# Revit family: 0047687 Lighting Fixture_Sylvania_Sylproof Superia LED_Surface Mounted
name_source: partatom
category: Lighting Fixtures
revit_build: Autodesk Revit 2015 (Build: 20140606_1530(x64)
units: mm (PartAtom-declared; Revit-internal decimal feet)

## types (1)
- SYLPROOF SUPERIA LED 665MM SINGLE NW
    Apparent Load = 12 VA
    Assembly Code = D5020200
    Body Material = Polycarbonate_Body_Sylvania_Brite White
    Bracket-Diffuser Material = <By Category>
    Bracket-Mounting Material = <By Category>
    CRI ( Ra ) = 85
    Catalog Number = 0047687 SYLPROOF SUPERIA LED 665MM SINGLE NW

LED
    Color Filter = 16777215
    Default Elevation = 0 mm  [stored 0 ft]
    Description = Weatherproof LED luminaire achieving up to 6,880lm (86lm/W); Linear prisms designed to optimise light output and to reduce glare;Extra long life with 50,000 hours; LED technology provides energy efficient solution and reduced maintenance costs.
    Diffuser Brackets Length = 505 mm  [stored 1.65682 ft]
    Diffuser Material = Polycarbonate_Diffuser_Sylvania_Clear
    Dimming Lamp Color Temperature Shift = <None>
    Emit Shape Visible in Rendering = No
    Emit from Rectangle Length = 645 mm  [stored 2.11614 ft]
    Emit from Rectangle Width = 66 mm
    Height = 98 mm  [stored 0.321522 ft]
    Housing ( Degree ) = 850 C
    IP rating = 65
    LOR Light Output Ratio ( % ) = 100 %
    Lamp = 12W LED
    Lamp - Single = Yes
    Lamp - Twin = No
    Lamp Comments = Integrated LED
    Lamp Material = Acrylic High Luminance Glass_Lamp_Sylvania_White
    Length = 665 mm  [stored 2.18176 ft]
    Length Help = 605 mm  [stored 1.98491 ft]
    Manufacturer = Feilo-Sylvania Group
    Model = SYLPROOF SUPERIA LED 665MM SINGLE NW
    Mounting Brackets Length = 390 mm  [stored 1.27953 ft]
    Mounting Brackets Width = 41 mm  [stored 0.134514 ft]
    Number of Diffuser Brackets = 3
    Photometric Web File = 0047687_SYLPROOFSUPERIALED12W4KNW-163341.ies
    Product Family = Sylproof Susperia LED
    Side Void Width = 45 mm  [stored 0.147638 ft]
    Tilt Angle = -90.00°
    Voltage = 240 V
    Voltage Comments = UNV (Universal Voltage; 220-240 Volt)
    Weight = 1.2 kg
    Width = 94 mm  [stored 0.308399 ft]
    Width Help = 26 mm

note: [stored X ft] marks values corroborated as IEEE doubles in the binary element streams (Revit-internal decimal feet)

## geometry (parser evidence)
native form markers: Blend x5, Sweep x14
no freeform markers — native parametric forms only
